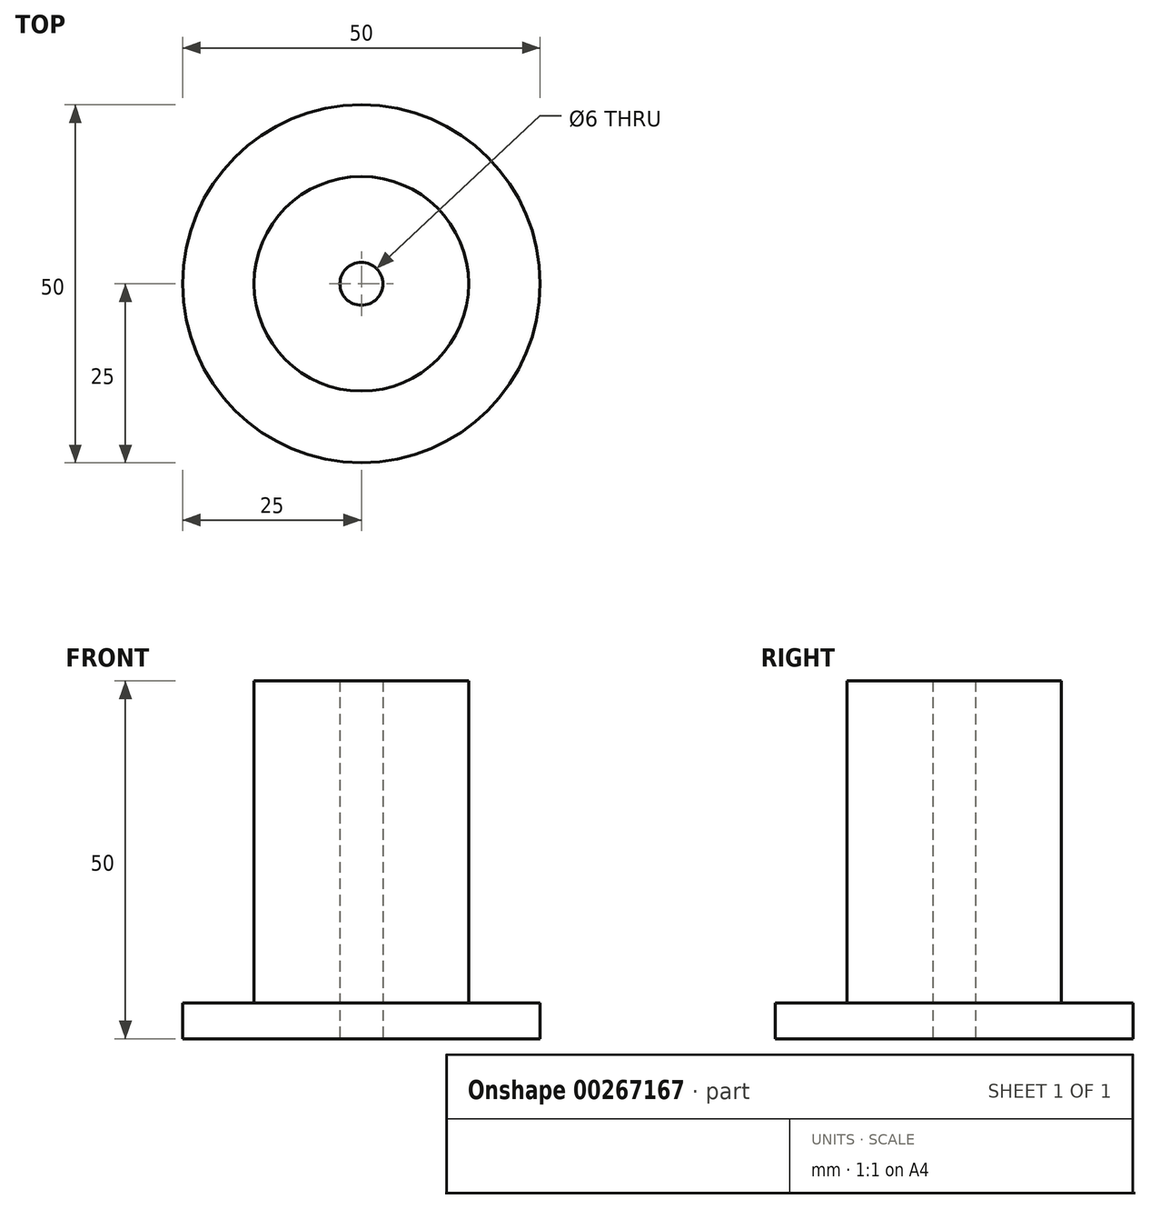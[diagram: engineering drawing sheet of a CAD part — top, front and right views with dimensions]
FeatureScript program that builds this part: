
annotation { "Feature Type Name" : "Feature", "Feature Type Description" : "" }
export const myFeature = defineFeature(function(context is Context, id is Id, definition is map)
    precondition{}
    {
        {
            var Q0;
            Q0=qCreatedBy(makeId("Top.planeOp"),FACE);
            var sketch = newSketch(context, id + "F0", { "sketchPlane" : qUnion([Q0])});
            skCircle(sketch, "E0", {"center": v(0, 0) * mm, "radius": 15 * mm});
            skSolve(sketch);
        }
        {
            var Q0;
            Q0 = qSketchRegion(id + "F0", true);
            extrude(context, id + "F1", {"entities" : qUnion([Q0]), "depth" : 50 * mm});
        }
        {
            var Q0;
            Q0=qCreatedBy(makeId("Top.planeOp"),FACE);
            var sketch = newSketch(context, id + "F2", { "sketchPlane" : qUnion([Q0])});
            skCircle(sketch, "E1", {"center": v(0, 0) * mm, "radius": 25 * mm});
            skSolve(sketch);
        }
        {
            var Q0;
            Q0 = qSketchRegion(id + "F2", true);
            extrude(context, id + "F3", {"entities" : qUnion([Q0]), "operationType" : NewBodyOperationType.ADD, "depth" : 5 * mm});
        }
        {
            var Q0;
            Q0=qCreatedBy(makeId("Top.planeOp"),FACE);
            var sketch = newSketch(context, id + "F4", { "sketchPlane" : qUnion([Q0])});
            skCircle(sketch, "E2", {"center": v(0, 0) * mm, "radius": 3 * mm});
            skSolve(sketch);
        }
        {
            var Q0;
            Q0 = qSketchRegion(id + "F4", true);
            extrude(context, id + "F5", {"entities" : qUnion([Q0]), "depth" : 60 * mm});
        }
        {
            var Q0;
            Q0=makeQuery(id+"F5.opExtrude","SWEPT_BODY",BODY,{"disambiguationData":[OSD([sQuery(id+"F4.wireOp",EDGE,"E2")])]});
            var Q1;
            Q1=makeQuery(id+"F1.opExtrude","SWEPT_BODY",BODY,{"disambiguationData":[OSD([sQuery(id+"F0.wireOp",EDGE,"E0")])]});
            booleanBodies(context, id + "F6", {"operationType" : BooleanOperationType.SUBTRACTION, "tools" : qUnion([Q0]), "targets" : qUnion([Q1])});
        }
    });
